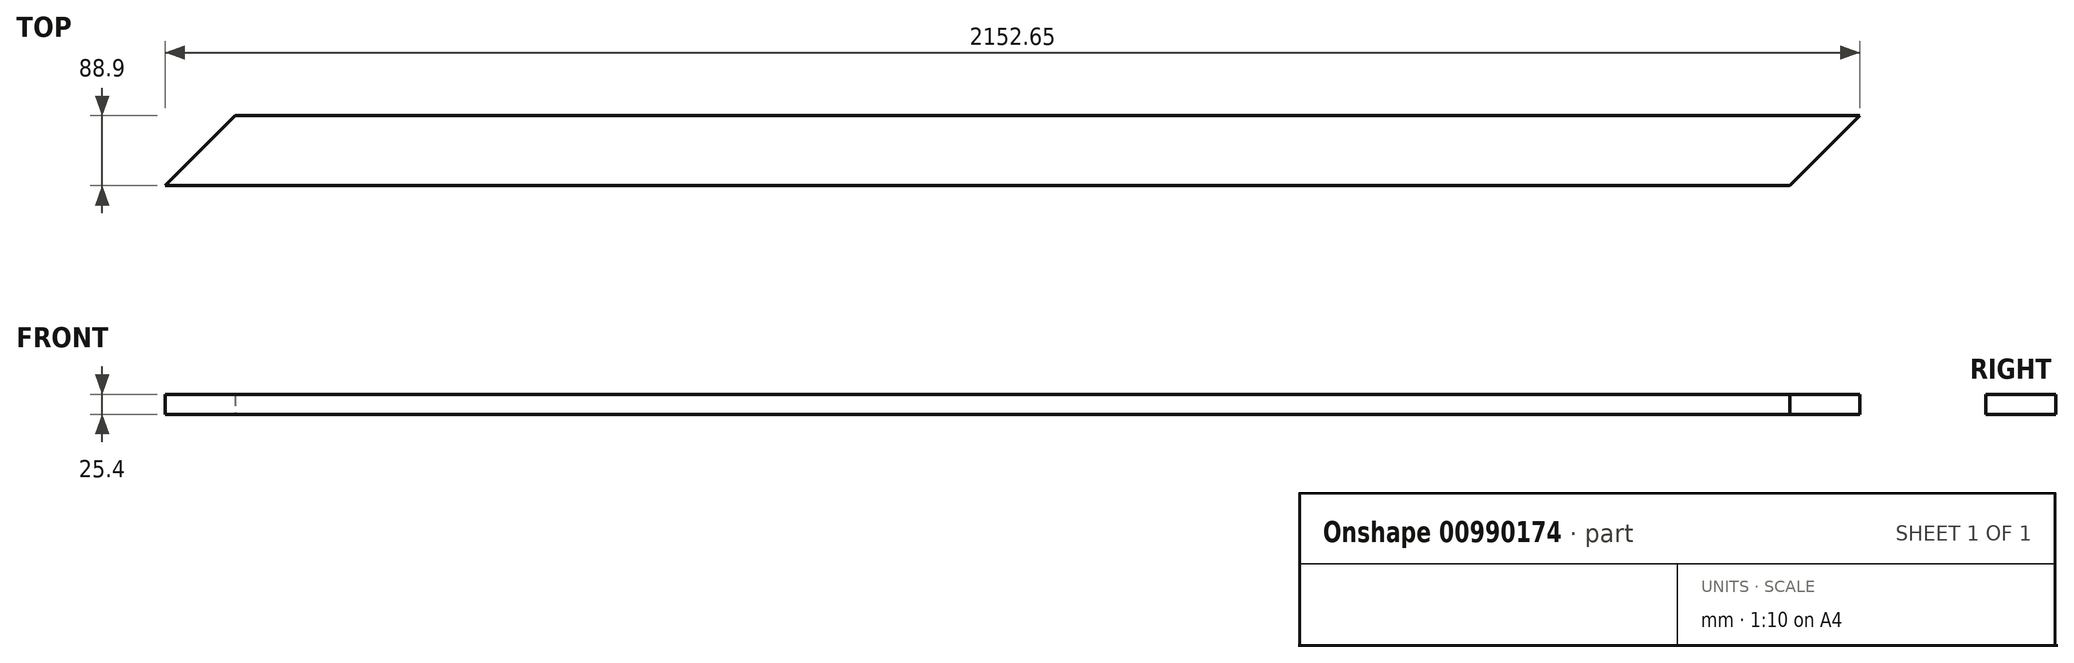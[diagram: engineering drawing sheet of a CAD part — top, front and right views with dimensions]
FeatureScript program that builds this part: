
annotation { "Feature Type Name" : "Feature", "Feature Type Description" : "" }
export const myFeature = defineFeature(function(context is Context, id is Id, definition is map)
    precondition{}
    {
        {
            var Q0;
            Q0=qCreatedBy(makeId("Top.planeOp"),FACE);
            var sketch = newSketch(context, id + "F0", { "sketchPlane" : qUnion([Q0])});
            skLineSegment(sketch, "E0.bottom", {"start": v(0, 0) * mm, "end": v(2152.65, 0) * mm});
            skLineSegment(sketch, "E0.top", {"start": v(0, 88.9) * mm, "end": v(2152.65, 88.9) * mm});
            skLineSegment(sketch, "E0.left", {"start": v(0, 0) * mm, "end": v(0, 88.9) * mm});
            skLineSegment(sketch, "E0.right", {"start": v(2152.65, 0) * mm, "end": v(2152.65, 88.9) * mm});
            skLineSegment(sketch, "E1", {"start": v(0, 0) * mm, "end": v(88.9, 88.9) * mm});
            skLineSegment(sketch, "E2", {"start": v(2152.65, 88.9) * mm, "end": v(2063.75, 0) * mm});
            skSolve(sketch);
        }
        {
            var Q0;
            {var subQ0=sQuery(id+"F0.wireOp",EDGE,"E1");Q0=makeQuery(id+"F0.imprint","IMPRINT",FACE,{"disambiguationData":[TD([[makeQuery(id+"F0.imprint","IMPRINT",EDGE,{"derivedFrom":subQ0}),-1.0]])]});}
            extrude(context, id + "F1", {"entities" : qUnion([Q0]), "depth" : 25.4 * mm, "offsetDistance" : 25.4 * mm});
        }
    });
